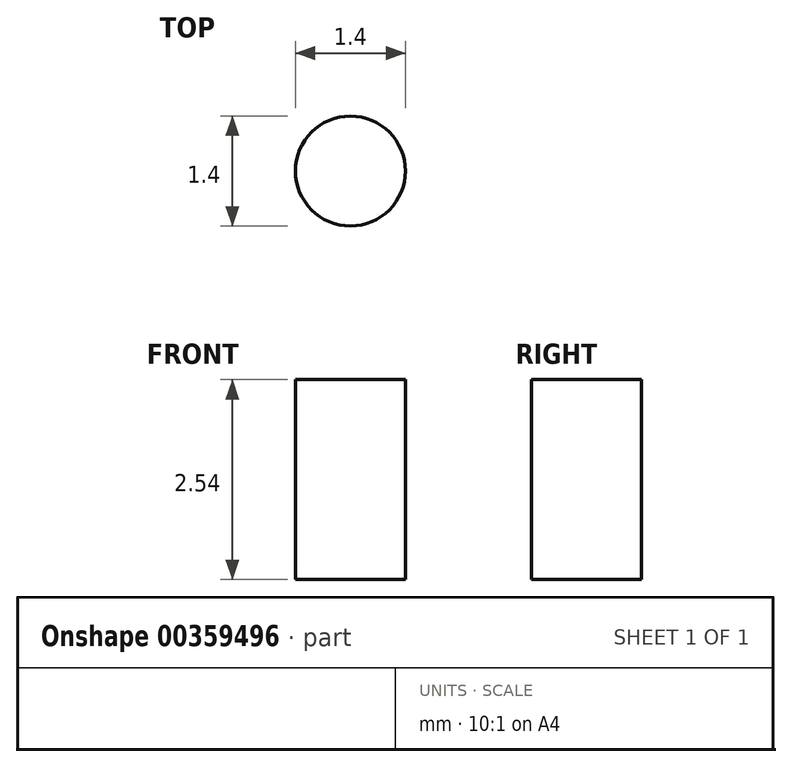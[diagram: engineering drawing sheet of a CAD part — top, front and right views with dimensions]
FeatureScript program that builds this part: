
annotation { "Feature Type Name" : "Feature", "Feature Type Description" : "" }
export const myFeature = defineFeature(function(context is Context, id is Id, definition is map)
    precondition{}
    {
        {
            var Q0;
            Q0=qCreatedBy(makeId("Top.planeOp"),FACE);
            var sketch = newSketch(context, id + "F0", { "sketchPlane" : qUnion([Q0])});
            skCircle(sketch, "E0", {"center": v(0, 0) * mm, "radius": 0.7 * mm});
            skSolve(sketch);
        }
        {
            var Q0;
            Q0 = qSketchRegion(id + "F0", true);
            extrude(context, id + "F1", {"entities" : qUnion([Q0]), "depth" : 2.54 * mm});
        }
    });
